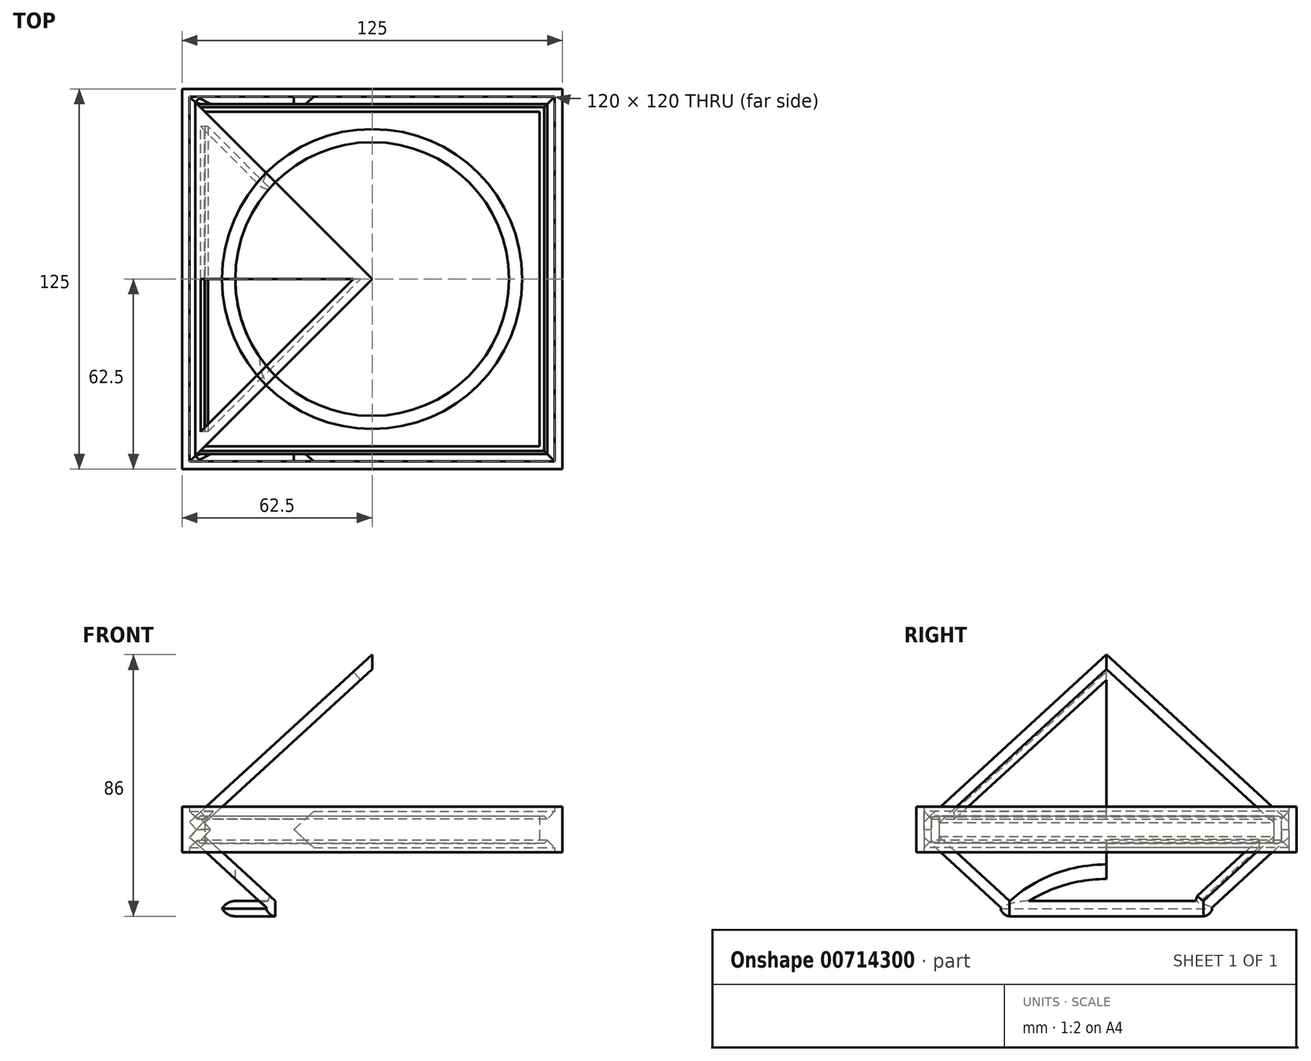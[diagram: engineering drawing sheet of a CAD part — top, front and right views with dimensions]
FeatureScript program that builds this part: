
annotation { "Feature Type Name" : "Feature", "Feature Type Description" : "" }
export const myFeature = defineFeature(function(context is Context, id is Id, definition is map)
    precondition{}
    {
        {
            var Q0;
            Q0=qCreatedBy(makeId("Top.planeOp"),FACE);
            var sketch = newSketch(context, id + "F0", { "sketchPlane" : qUnion([Q0])});
            skLineSegment(sketch, "E0.bottom", {"start": v(-60, 60) * mm, "end": v(60, 60) * mm});
            skLineSegment(sketch, "E0.top", {"start": v(-60, -60) * mm, "end": v(60, -60) * mm});
            skLineSegment(sketch, "E0.left", {"start": v(-60, 60) * mm, "end": v(-60, -60) * mm});
            skLineSegment(sketch, "E0.right", {"start": v(60, 60) * mm, "end": v(60, -60) * mm});
            skPoint(sketch, "E0.middle", {"position": v(0, 0) * mm});
            skLineSegment(sketch, "E1.bottom", {"start": v(-57.5, 57.5) * mm, "end": v(57.5, 57.5) * mm});
            skLineSegment(sketch, "E1.top", {"start": v(-57.5, -57.5) * mm, "end": v(57.5, -57.5) * mm});
            skLineSegment(sketch, "E1.left", {"start": v(-57.5, 57.5) * mm, "end": v(-57.5, -57.5) * mm});
            skLineSegment(sketch, "E1.right", {"start": v(57.5, 57.5) * mm, "end": v(57.5, -57.5) * mm});
            skLineSegment(sketch, "E2.bottom", {"start": v(-62.5, 62.5) * mm, "end": v(62.5, 62.5) * mm});
            skLineSegment(sketch, "E2.top", {"start": v(-62.5, -62.5) * mm, "end": v(62.5, -62.5) * mm});
            skLineSegment(sketch, "E2.left", {"start": v(-62.5, 62.5) * mm, "end": v(-62.5, -62.5) * mm});
            skLineSegment(sketch, "E2.right", {"start": v(62.5, 62.5) * mm, "end": v(62.5, -62.5) * mm});
            skLineSegment(sketch, "E3.bottom", {"start": v(-55, 55) * mm, "end": v(55, 55) * mm});
            skLineSegment(sketch, "E3.top", {"start": v(-55, -55) * mm, "end": v(55, -55) * mm});
            skLineSegment(sketch, "E3.left", {"start": v(-55, 55) * mm, "end": v(-55, -55) * mm});
            skLineSegment(sketch, "E3.right", {"start": v(55, 55) * mm, "end": v(55, -55) * mm});
            skSolve(sketch);
        }
        {
            var Q0;
            Q0=makeQuery(id+"F0.imprint","IMPRINT",FACE,{"disambiguationData":[TD([[makeQuery(id+"F0.imprint","IMPRINT",EDGE,{"derivedFrom":sQuery(id+"F0.wireOp",EDGE,"E0.bottom")}),-1.0]])]});
            extrude(context, id + "F1", {"entities" : qUnion([Q0]), "endBound" : BoundingType.SYMMETRIC, "depth" : 12 * mm, "offsetDistance" : 25 * mm});
        }
        {
            var Q0;
            Q0=makeQuery(id+"F1.opExtrude","CAP_EDGE",EDGE,{"disambiguationData":[OSD([sQuery(id+"F0.wireOp",EDGE,"E1.top")])],"isStart":false});
            var Q1;
            Q1=makeQuery(id+"F1.opExtrude","CAP_EDGE",EDGE,{"disambiguationData":[OSD([sQuery(id+"F0.wireOp",EDGE,"E1.left")])],"isStart":false});
            var Q2;
            Q2=makeQuery(id+"F1.opExtrude","CAP_EDGE",EDGE,{"disambiguationData":[OSD([sQuery(id+"F0.wireOp",EDGE,"E1.right")])],"isStart":false});
            var Q3;
            Q3=makeQuery(id+"F1.opExtrude","CAP_EDGE",EDGE,{"disambiguationData":[OSD([sQuery(id+"F0.wireOp",EDGE,"E1.bottom")])],"isStart":false});
            var Q4;
            Q4=makeQuery(id+"F1.opExtrude","CAP_EDGE",EDGE,{"disambiguationData":[OSD([sQuery(id+"F0.wireOp",EDGE,"E1.right")])],"isStart":true});
            var Q5;
            Q5=makeQuery(id+"F1.opExtrude","CAP_EDGE",EDGE,{"disambiguationData":[OSD([sQuery(id+"F0.wireOp",EDGE,"E1.bottom")])],"isStart":true});
            var Q6;
            Q6=makeQuery(id+"F1.opExtrude","CAP_EDGE",EDGE,{"disambiguationData":[OSD([sQuery(id+"F0.wireOp",EDGE,"E1.top")])],"isStart":true});
            var Q7;
            Q7=makeQuery(id+"F1.opExtrude","CAP_EDGE",EDGE,{"disambiguationData":[OSD([sQuery(id+"F0.wireOp",EDGE,"E1.left")])],"isStart":true});
            chamfer(context, id + "F2", {"entities" : qUnion([Q0, Q1, Q2, Q3, Q4, Q5, Q6, Q7]), "chamferType" : ChamferType.OFFSET_ANGLE, "width" : 2.5 * mm, "oppositeDirection" : false, "angle" : 45 * degree, "tangentPropagation" : true});
        }
        {
            var Q0;
            Q0=qCreatedBy(makeId("Front.planeOp"),FACE);
            var sketch = newSketch(context, id + "F3", { "sketchPlane" : qUnion([Q0])});
            skLineSegment(sketch, "E4", {"start": v(0, 0) * mm, "end": v(0, -2.5) * mm});
            skLineSegment(sketch, "E5", {"start": v(0, -2.5) * mm, "end": v(-60, -2.5) * mm});
            skLineSegment(sketch, "E6", {"start": v(0, -2.5) * mm, "end": v(0, -57.5) * mm});
            skLineSegment(sketch, "E7", {"start": v(-60, -2.5) * mm, "end": v(0, -57.5) * mm});
            skLineSegment(sketch, "E8", {"start": v(0, 0) * mm, "end": v(-57.5, 0) * mm});
            skLineSegment(sketch, "E9", {"start": v(-57.5, 0) * mm, "end": v(0, -52.7) * mm});
            skLineSegment(sketch, "E10", {"start": v(-60, -2.5) * mm, "end": v(-57.5, 0) * mm});
            skLineSegment(sketch, "E11.MirrorCS", {"start": v(0, 0) * mm, "end": v(0, 2.5) * mm});
            skLineSegment(sketch, "E12.MirrorCS", {"start": v(0, 2.5) * mm, "end": v(0, 57.5) * mm});
            skLineSegment(sketch, "E13.MirrorCS", {"start": v(-57.5, 0) * mm, "end": v(0, 52.7) * mm});
            skLineSegment(sketch, "E14.MirrorCS", {"start": v(-60, 2.5) * mm, "end": v(0, 57.5) * mm});
            skLineSegment(sketch, "E15.MirrorCS", {"start": v(-60, 2.5) * mm, "end": v(-57.5, 0) * mm});
            skSolve(sketch);
        }
        {
            var Q0;
            {var subQ0=sQuery(id+"F3.wireOp",EDGE,"E7");Q0=makeQuery(id+"F3.imprint","IMPRINT",FACE,{"disambiguationData":[TD([[makeQuery(id+"F3.imprint","IMPRINT",EDGE,{"derivedFrom":subQ0}),1.0]])]});}
            var Q1;
            {var subQ0=sQuery(id+"F3.wireOp",EDGE,"E10");Q1=makeQuery(id+"F3.imprint","IMPRINT",FACE,{"disambiguationData":[TD([[makeQuery(id+"F3.imprint","IMPRINT",EDGE,{"derivedFrom":subQ0}),-1.0]])]});}
            extrude(context, id + "F4", {"entities" : qUnion([Q0, Q1]), "endBound" : BoundingType.SYMMETRIC, "depth" : 120 * mm, "offsetDistance" : 25 * mm});
        }
        {
            var Q0;
            Q0=makeQuery(id+"F4.opExtrude","SWEPT_FACE",FACE,{"disambiguationData":[OSD([sQuery(id+"F3.wireOp",EDGE,"E7")])]});
            cPlane(context, id + "F5", {"entities" : qUnion([Q0]), "cplaneType" : CPlaneType.OFFSET, "offset" : 0 * mm, "width" : 150 * mm, "height" : 150 * mm});
        }
        {
            var Q0;
            Q0=qCreatedBy(id+"F5.planeOp",FACE);
            var sketch = newSketch(context, id + "F6", { "sketchPlane" : qUnion([Q0])});
            skLineSegment(sketch, "E16", {"start": v(0, 0) * mm, "end": v(-42.54, 0) * mm});
            skLineSegment(sketch, "E17", {"start": v(-42.54, 0) * mm, "end": v(-42.54, -60) * mm});
            skLineSegment(sketch, "E18", {"start": v(-42.54, -60) * mm, "end": v(38.85, 0) * mm});
            skLineSegment(sketch, "E19.MirrorCS", {"start": v(-42.54, 0) * mm, "end": v(-42.54, 60) * mm});
            skPoint(sketch, "E20.MirrorCS.end.orphan", {"position": v(38.85, 0) * mm});
            skPoint(sketch, "E20.MirrorCS.start.orphan", {"position": v(-42.54, 60) * mm});
            skLineSegment(sketch, "E21", {"start": v(-42.54, -60) * mm, "end": v(38.85, -60) * mm});
            skLineSegment(sketch, "E22", {"start": v(38.85, -60) * mm, "end": v(38.85, 0) * mm});
            skLineSegment(sketch, "E23.MirrorCS", {"start": v(-42.54, 60) * mm, "end": v(38.85, 0) * mm});
            skLineSegment(sketch, "E24.MirrorCS", {"start": v(38.85, 60) * mm, "end": v(38.85, 0) * mm});
            skLineSegment(sketch, "E25.MirrorCS", {"start": v(-42.54, 60) * mm, "end": v(38.85, 60) * mm});
            skLineSegment(sketch, "E26", {"start": v(-37.54, 0) * mm, "end": v(-37.54, -50.1) * mm});
            skLineSegment(sketch, "E27", {"start": v(0, 0) * mm, "end": v(30.43, 0) * mm});
            skLineSegment(sketch, "E28", {"start": v(-37.54, -50.1) * mm, "end": v(30.43, 0) * mm});
            skLineSegment(sketch, "E29", {"start": v(-37.54, 0) * mm, "end": v(30.43, 0) * mm});
            skLineSegment(sketch, "E30.MirrorCS", {"start": v(-37.54, 0) * mm, "end": v(-37.54, 50.1) * mm});
            skLineSegment(sketch, "E31.MirrorCS", {"start": v(-37.54, 50.1) * mm, "end": v(30.43, 0) * mm});
            skSolve(sketch);
        }
        {
            var Q0;
            Q0=makeQuery(id+"F6.imprint","IMPRINT",FACE,{"disambiguationData":[TD([[makeQuery(id+"F6.imprint","IMPRINT",EDGE,{"derivedFrom":sQuery(id+"F6.wireOp",EDGE,"E23.MirrorCS")}),1.0]])]});
            var Q1;
            Q1=makeQuery(id+"F6.imprint","IMPRINT",FACE,{"disambiguationData":[TD([[makeQuery(id+"F6.imprint","IMPRINT",EDGE,{"derivedFrom":sQuery(id+"F6.wireOp",EDGE,"E18")}),-1.0]])]});
            var Q2;
            Q2=makeQuery(id+"F6.imprint","IMPRINT",FACE,{"disambiguationData":[TD([[makeQuery(id+"F6.imprint","IMPRINT",EDGE,{"derivedFrom":sQuery(id+"F6.wireOp",EDGE,"E26")}),1.0]])]});
            var Q3;
            Q3=makeQuery(id+"F6.imprint","IMPRINT",FACE,{"disambiguationData":[TD([[makeQuery(id+"F6.imprint","IMPRINT",EDGE,{"derivedFrom":sQuery(id+"F6.wireOp",EDGE,"E29")}),1.0]])]});
            extrude(context, id + "F7", {"entities" : qUnion([Q0, Q1, Q2, Q3]), "operationType" : NewBodyOperationType.REMOVE, "oppositeDirection" : true, "depth" : 25 * mm, "offsetDistance" : 25 * mm});
        }
        {
            var Q0;
            {var subQ2=sQuery(id+"F3.wireOp",EDGE,"E13.MirrorCS");Q0=makeQuery(id+"F3.imprint","IMPRINT",FACE,{"disambiguationData":[TD([[makeQuery(id+"F3.imprint","IMPRINT",EDGE,{"derivedFrom":subQ2}),1.0]])]});}
            extrude(context, id + "F8", {"entities" : qUnion([Q0]), "endBound" : BoundingType.SYMMETRIC, "depth" : 120 * mm, "offsetDistance" : 25 * mm});
        }
        {
            var Q0;
            Q0=makeQuery(id+"F8.opExtrude","SWEPT_FACE",FACE,{"disambiguationData":[OSD([sQuery(id+"F3.wireOp",EDGE,"E14.MirrorCS")])]});
            cPlane(context, id + "F9", {"entities" : qUnion([Q0]), "cplaneType" : CPlaneType.OFFSET, "offset" : 0 * mm, "width" : 150 * mm, "height" : 150 * mm});
        }
        {
            var Q0;
            Q0=qCreatedBy(id+"F9.planeOp",FACE);
            var sketch = newSketch(context, id + "F10", { "sketchPlane" : qUnion([Q0])});
            skLineSegment(sketch, "E32", {"start": v(0, 0) * mm, "end": v(-42.54, 0) * mm});
            skLineSegment(sketch, "E33", {"start": v(-42.54, 0) * mm, "end": v(-42.54, -60) * mm});
            skLineSegment(sketch, "E34", {"start": v(-42.54, -60) * mm, "end": v(38.85, 0) * mm});
            skLineSegment(sketch, "E35.MirrorCS", {"start": v(-42.54, 0) * mm, "end": v(-42.54, 60) * mm});
            skPoint(sketch, "E36.MirrorCS.end.orphan", {"position": v(38.85, 0) * mm});
            skPoint(sketch, "E36.MirrorCS.start.orphan", {"position": v(-42.54, 60) * mm});
            skLineSegment(sketch, "E37", {"start": v(-42.54, -60) * mm, "end": v(38.85, -60) * mm});
            skLineSegment(sketch, "E38", {"start": v(38.85, -60) * mm, "end": v(38.85, 0) * mm});
            skLineSegment(sketch, "E39.MirrorCS", {"start": v(-42.54, 60) * mm, "end": v(38.85, 0) * mm});
            skLineSegment(sketch, "E40.MirrorCS", {"start": v(38.85, 60) * mm, "end": v(38.85, 0) * mm});
            skLineSegment(sketch, "E41.MirrorCS", {"start": v(-42.54, 60) * mm, "end": v(38.85, 60) * mm});
            skLineSegment(sketch, "E42", {"start": v(-37.54, 0) * mm, "end": v(-37.54, -50.1) * mm});
            skLineSegment(sketch, "E43", {"start": v(0, 0) * mm, "end": v(30.43, 0) * mm});
            skLineSegment(sketch, "E44", {"start": v(-37.54, -50.1) * mm, "end": v(30.43, 0) * mm});
            skLineSegment(sketch, "E45", {"start": v(-37.54, 0) * mm, "end": v(30.43, 0) * mm});
            skLineSegment(sketch, "E46.MirrorCS", {"start": v(-37.54, 0) * mm, "end": v(-37.54, 50.1) * mm});
            skLineSegment(sketch, "E47.MirrorCS", {"start": v(-37.54, 50.1) * mm, "end": v(30.43, 0) * mm});
            skSolve(sketch);
        }
        {
            var Q0;
            Q0=makeQuery(id+"F10.imprint","IMPRINT",FACE,{"disambiguationData":[TD([[makeQuery(id+"F10.imprint","IMPRINT",EDGE,{"derivedFrom":sQuery(id+"F10.wireOp",EDGE,"E39.MirrorCS")}),1.0]])]});
            var Q1;
            Q1=makeQuery(id+"F10.imprint","IMPRINT",FACE,{"disambiguationData":[TD([[makeQuery(id+"F10.imprint","IMPRINT",EDGE,{"derivedFrom":sQuery(id+"F10.wireOp",EDGE,"E34")}),-1.0]])]});
            var Q2;
            Q2=makeQuery(id+"F10.imprint","IMPRINT",FACE,{"disambiguationData":[TD([[makeQuery(id+"F10.imprint","IMPRINT",EDGE,{"derivedFrom":sQuery(id+"F10.wireOp",EDGE,"E42")}),1.0]])]});
            var Q3;
            Q3=makeQuery(id+"F10.imprint","IMPRINT",FACE,{"disambiguationData":[TD([[makeQuery(id+"F10.imprint","IMPRINT",EDGE,{"derivedFrom":sQuery(id+"F10.wireOp",EDGE,"E45")}),1.0]])]});
            extrude(context, id + "F11", {"entities" : qUnion([Q0, Q1, Q2, Q3]), "operationType" : NewBodyOperationType.REMOVE, "oppositeDirection" : true, "depth" : 25 * mm, "offsetDistance" : 25 * mm});
        }
        {
            var Q0;
            Q0=makeQuery(id+"F7.boolean.opBoolean","INTERSECT",EDGE,{"derivedFrom":[makeQuery(id+"F4.opExtrude","SWEPT_FACE",FACE,{"disambiguationData":[OSD([sQuery(id+"F3.wireOp",EDGE,"E9")])]}),makeQuery(id+"F7.opExtrude","SWEPT_FACE",FACE,{"disambiguationData":[OSD([sQuery(id+"F6.wireOp",EDGE,"E18")])]})]});
            var Q1;
            Q1=makeQuery(id+"F7.boolean.opBoolean","INTERSECT",EDGE,{"derivedFrom":[makeQuery(id+"F4.opExtrude","SWEPT_FACE",FACE,{"disambiguationData":[OSD([sQuery(id+"F3.wireOp",EDGE,"E9")])]}),makeQuery(id+"F7.opExtrude","SWEPT_FACE",FACE,{"disambiguationData":[OSD([sQuery(id+"F6.wireOp",EDGE,"E23.MirrorCS")])]})]});
            var Q2;
            Q2=makeQuery(id+"F11.boolean.opBoolean","INTERSECT",EDGE,{"derivedFrom":[makeQuery(id+"F8.opExtrude","SWEPT_FACE",FACE,{"disambiguationData":[OSD([sQuery(id+"F3.wireOp",EDGE,"E13.MirrorCS")])]}),makeQuery(id+"F11.opExtrude","SWEPT_FACE",FACE,{"disambiguationData":[OSD([sQuery(id+"F10.wireOp",EDGE,"E39.MirrorCS")])]})]});
            var Q3;
            Q3=makeQuery(id+"F11.boolean.opBoolean","INTERSECT",EDGE,{"derivedFrom":[makeQuery(id+"F8.opExtrude","SWEPT_FACE",FACE,{"disambiguationData":[OSD([sQuery(id+"F3.wireOp",EDGE,"E13.MirrorCS")])]}),makeQuery(id+"F11.opExtrude","SWEPT_FACE",FACE,{"disambiguationData":[OSD([sQuery(id+"F10.wireOp",EDGE,"E34")])]})]});
            chamfer(context, id + "F12", {"entities" : qUnion([Q0, Q1, Q2, Q3]), "chamferType" : ChamferType.OFFSET_ANGLE, "width" : 1.92 * mm, "oppositeDirection" : false, "angle" : 61.5 * degree, "tangentPropagation" : true});
        }
        {
            var Q0;
            Q0=qCreatedBy(makeId("Top.planeOp"),FACE);
            var sketch = newSketch(context, id + "F13", { "sketchPlane" : qUnion([Q0])});
            skCircle(sketch, "E48", {"center": v(0, 0) * mm, "radius": 45 * mm});
            skSolve(sketch);
        }
        {
            var Q0;
            Q0=makeQuery(id+"F13.imprint","IMPRINT",FACE,{"disambiguationData":[TD([[makeQuery(id+"F13.imprint","IMPRINT",EDGE,{"derivedFrom":sQuery(id+"F13.wireOp",EDGE,"E48")}),1.0]])]});
            extrude(context, id + "F14", {"entities" : qUnion([Q0]), "operationType" : NewBodyOperationType.REMOVE, "oppositeDirection" : true, "depth" : 65.2 * mm, "offsetDistance" : 25 * mm});
        }
        {
            var Q0;
            Q0=qCreatedBy(makeId("Top.planeOp"),FACE);
            cPlane(context, id + "F15", {"entities" : qUnion([Q0]), "cplaneType" : CPlaneType.OFFSET, "offset" : 26 * mm, "oppositeDirection" : true, "width" : 150 * mm, "height" : 150 * mm});
        }
        {
            var Q0;
            Q0=qCreatedBy(id+"F15.planeOp",FACE);
            var sketch = newSketch(context, id + "F16", { "sketchPlane" : qUnion([Q0])});
            skArc(sketch, "E49", {"start": v(-31.82, 31.82) * mm, "mid": v(-45, 0) * mm, "end": v(-31.82, -31.82) * mm});
            skArc(sketch, "E50", {"start": v(-35.36, 35.36) * mm, "mid": v(-50, 0) * mm, "end": v(-35.36, -35.36) * mm});
            skLineSegment(sketch, "E51", {"start": v(0, 0) * mm, "end": v(0, 60) * mm});
            skLineSegment(sketch, "E52", {"start": v(0, 60) * mm, "end": v(-60, 60) * mm});
            skLineSegment(sketch, "E53", {"start": v(0, 0) * mm, "end": v(-35.36, 35.36) * mm});
            skLineSegment(sketch, "E54", {"start": v(0, 0) * mm, "end": v(-36.87, 0) * mm});
            skLineSegment(sketch, "E55.MirrorCS", {"start": v(0, 0) * mm, "end": v(-60, -60) * mm});
            skSolve(sketch);
        }
        {
            var Q0;
            {var subQ0=sQuery(id+"F16.wireOp",EDGE,"E49");Q0=makeQuery(id+"F16.imprint","IMPRINT",FACE,{"disambiguationData":[TD([[makeQuery(id+"F16.imprint","IMPRINT",EDGE,{"derivedFrom":subQ0}),-1.0]])]});}
            extrude(context, id + "F17", {"entities" : qUnion([Q0]), "operationType" : NewBodyOperationType.ADD, "endBound" : BoundingType.SYMMETRIC, "depth" : 5 * mm, "offsetDistance" : 25 * mm});
        }
        {
            var Q0;
            Q0=makeQuery(id+"F17.opExtrude","CAP_EDGE",EDGE,{"disambiguationData":[OSD([sQuery(id+"F16.wireOp",EDGE,"E50")])],"isStart":false});
            var Q1;
            Q1=makeQuery(id+"F17.opExtrude","CAP_EDGE",EDGE,{"disambiguationData":[OSD([sQuery(id+"F16.wireOp",EDGE,"E50")])],"isStart":true});
            fillet(context, id + "F18", {"entities" : qUnion([Q0, Q1]), "radius" : 5 * mm, "tangentPropagation" : true, "allowEdgeOverflow" : false});
        }
        {
            var Q0;
            Q0=makeQuery(id+"F0.imprint","IMPRINT",FACE,{"disambiguationData":[TD([[makeQuery(id+"F0.imprint","IMPRINT",EDGE,{"derivedFrom":sQuery(id+"F0.wireOp",EDGE,"E0.bottom")}),1.0]])]});
            extrude(context, id + "F19", {"entities" : qUnion([Q0]), "operationType" : NewBodyOperationType.ADD, "endBound" : BoundingType.SYMMETRIC, "depth" : 15 * mm, "offsetDistance" : 25 * mm});
        }
        {
            var Q0;
            Q0=makeQuery(id+"F0.imprint","IMPRINT",FACE,{"disambiguationData":[TD([[makeQuery(id+"F0.imprint","IMPRINT",EDGE,{"derivedFrom":sQuery(id+"F0.wireOp",EDGE,"E1.bottom")}),-1.0]])]});
            extrude(context, id + "F20", {"entities" : qUnion([Q0]), "operationType" : NewBodyOperationType.ADD, "endBound" : BoundingType.SYMMETRIC, "depth" : 9 * mm, "offsetDistance" : 25 * mm});
        }
        {
            var Q0;
            Q0=makeQuery(id+"F20.opExtrude","CAP_EDGE",EDGE,{"disambiguationData":[OSD([sQuery(id+"F0.wireOp",EDGE,"E1.left")])],"isStart":false});
            var Q1;
            Q1=makeQuery(id+"F20.opExtrude","CAP_EDGE",EDGE,{"disambiguationData":[OSD([sQuery(id+"F0.wireOp",EDGE,"E1.top")])],"isStart":false});
            var Q2;
            Q2=makeQuery(id+"F20.opExtrude","CAP_EDGE",EDGE,{"disambiguationData":[OSD([sQuery(id+"F0.wireOp",EDGE,"E1.right")])],"isStart":false});
            var Q3;
            Q3=makeQuery(id+"F20.opExtrude","CAP_EDGE",EDGE,{"disambiguationData":[OSD([sQuery(id+"F0.wireOp",EDGE,"E1.bottom")])],"isStart":false});
            var Q4;
            Q4=makeQuery(id+"F20.opExtrude","CAP_EDGE",EDGE,{"disambiguationData":[OSD([sQuery(id+"F0.wireOp",EDGE,"E1.left")])],"isStart":true});
            var Q5;
            Q5=makeQuery(id+"F20.opExtrude","CAP_EDGE",EDGE,{"disambiguationData":[OSD([sQuery(id+"F0.wireOp",EDGE,"E1.top")])],"isStart":true});
            var Q6;
            Q6=makeQuery(id+"F20.opExtrude","CAP_EDGE",EDGE,{"disambiguationData":[OSD([sQuery(id+"F0.wireOp",EDGE,"E1.right")])],"isStart":true});
            var Q7;
            Q7=makeQuery(id+"F20.opExtrude","CAP_EDGE",EDGE,{"disambiguationData":[OSD([sQuery(id+"F0.wireOp",EDGE,"E1.bottom")])],"isStart":true});
            chamfer(context, id + "F21", {"entities" : qUnion([Q0, Q1, Q2, Q3, Q4, Q5, Q6, Q7]), "width" : 1 * mm, "tangentPropagation" : true});
        }
    });
